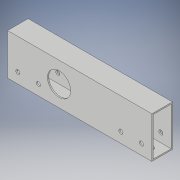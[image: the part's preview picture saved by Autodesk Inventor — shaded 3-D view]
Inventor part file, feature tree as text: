
AUTODESK INVENTOR PART (.ipt)
format: ipt  version: 2018 (Build 220112000, 112)  size: 128,512 bytes
history: native  units: in
note: dims shown in document units (in); Inventor stores cm internally (conversion verified against a paired STEP export)
features: hole x7, sketch x2, extrude x1, shell x1
ambient origin geometry x8: Origin, YZ Plane, XZ Plane, XY Plane, X Axis, Y Axis, Z Axis, Center Point
bodies: Solid1 (feature_tree)
feature tree (11):
  extrude  "Extrusion1"  Depth=2.0in
  shell  "Shell1"  Thickness=1.0in
  hole  "Hole1"  [1 undecoded]
  hole  "Hole2"  [1 undecoded]
  hole  "Hole3"  [1 undecoded]
  hole  "Hole4"  [1 undecoded]
  hole  "Hole5"  [1 undecoded]
  hole  "Hole6"  [1 undecoded]
  hole  "Hole7"  [1 undecoded]
  sketch  "Sketch1"  dims[d0=7.0in d1=2.0in d2=1.0in d3=0.0in]
  sketch  "Sketch2"  dims[d4=0.0625in d5=2.5in d6=1.125in d7=0.75in d8=0.375in d9=0.25in d10=0.5635in d11=1.0in d12=0.8108in d13=1.0in d14=0.5in d15=0.5in d16=0.2031in d17=0.75in d18=0.375in d19=0.25in d20=0.5635in d21=1.0in d22=0.8108in d23=1.5in d24=0.5in d25=0.2031in d26=0.75in d27=0.375in d28=0.25in d29=0.5635in d30=1.0in d31=0.8108in d32=0.5in d33=0.5in d34=0.2031in d35=0.75in d36=0.375in d37=0.25in d38=0.5635in d39=1.0in d40=0.8108in d41=1.5in d42=0.5in d43=0.2031in d44=0.75in d45=0.375in d46=0.25in d47=0.5635in d48=1.0in d49=0.8108in d50=0.5in d51=0.5in d52=0.2031in d53=0.75in d54=0.375in d55=0.25in d56=0.5635in d57=0.0625in d58=0.8108in d59=0.5in d60=0.5in d61=0.2031in d62=0.75in d63=0.375in d64=0.25in d65=0.5635in d66=0.125in d67=0.8108in]
note: 7 required parameter values undecoded (feature->parameter linkage not recoverable at this tier; creation-order binding heuristic only, values carry confidence <= 0.55)
